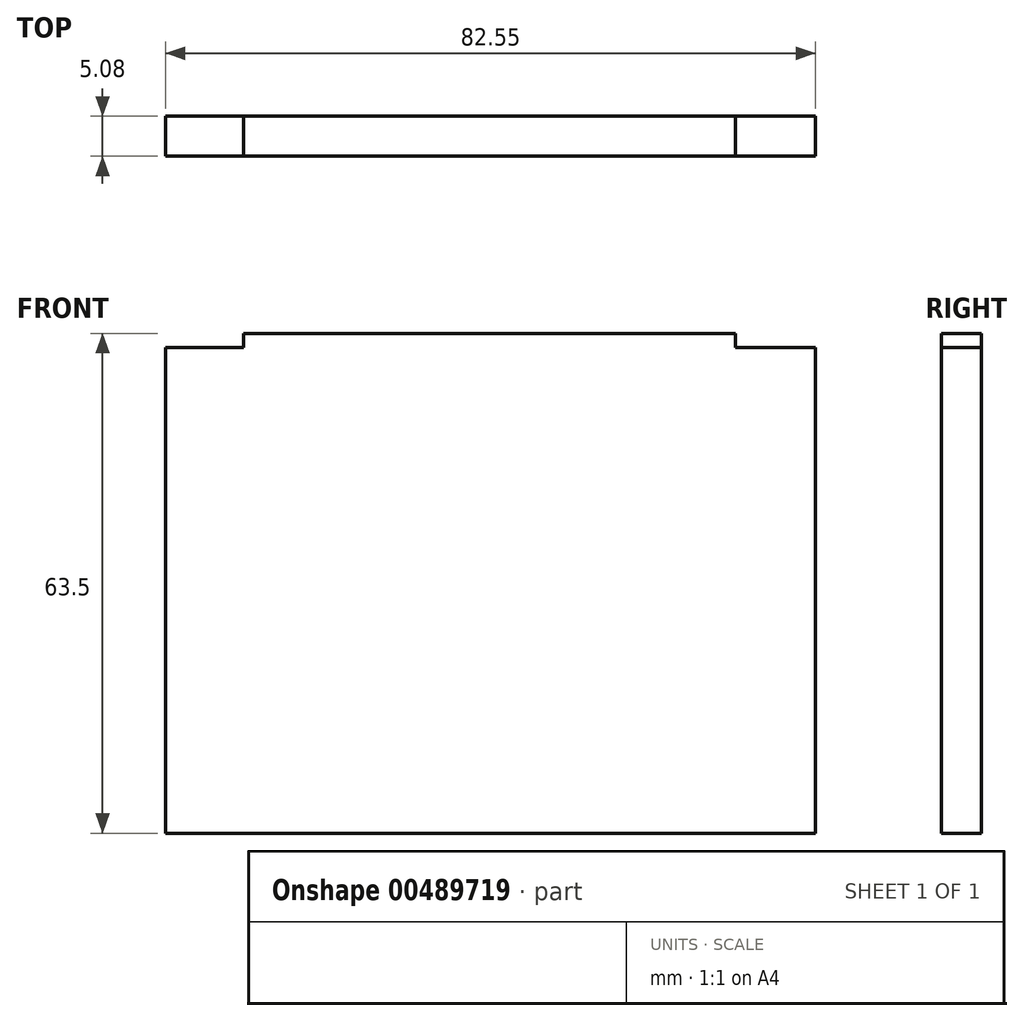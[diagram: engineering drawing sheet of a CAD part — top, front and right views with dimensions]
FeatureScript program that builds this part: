
annotation { "Feature Type Name" : "Feature", "Feature Type Description" : "" }
export const myFeature = defineFeature(function(context is Context, id is Id, definition is map)
    precondition{}
    {
        {
            var Q0;
            Q0=qCreatedBy(makeId("Front.planeOp"),FACE);
            var sketch = newSketch(context, id + "F0", { "sketchPlane" : qUnion([Q0])});
            skLineSegment(sketch, "E0.bottom", {"start": v(-43.78, -52.22) * mm, "end": v(38.77, -52.22) * mm});
            skLineSegment(sketch, "E0.top", {"start": v(-43.78, 9.5) * mm, "end": v(-33.87, 9.5) * mm});
            skLineSegment(sketch, "E0.left", {"start": v(-43.78, -52.22) * mm, "end": v(-43.78, 9.5) * mm});
            skLineSegment(sketch, "E0.right", {"start": v(38.77, -52.22) * mm, "end": v(38.77, 9.5) * mm});
            skLineSegment(sketch, "E1", {"start": v(38.77, 9.5) * mm, "end": v(28.87, 9.5) * mm});
            skLineSegment(sketch, "E2.top", {"start": v(-33.87, 11.28) * mm, "end": v(28.6, 11.28) * mm});
            skLineSegment(sketch, "E2.left", {"start": v(-33.87, 9.5) * mm, "end": v(-33.87, 11.28) * mm});
            skLineSegment(sketch, "E2.right", {"start": v(28.6, 9.5) * mm, "end": v(28.6, 11.28) * mm});
            skLineSegment(sketch, "E3.trimOffspring", {"start": v(28.6, 9.5) * mm, "end": v(38.77, 9.5) * mm});
            skSolve(sketch);
        }
        {
            var Q0;
            Q0=makeQuery(id+"F0.imprint","IMPRINT",FACE,{"disambiguationData":[TD([[makeQuery(id+"F0.imprint","IMPRINT",EDGE,{"derivedFrom":sQuery(id+"F0.wireOp",EDGE,"E0.bottom")}),1.0]])]});
            extrude(context, id + "F1", {"entities" : qUnion([Q0]), "depth" : 5.08 * mm});
        }
    });
